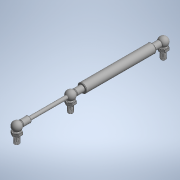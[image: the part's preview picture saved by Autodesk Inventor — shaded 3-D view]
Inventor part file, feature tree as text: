
AUTODESK INVENTOR PART (.ipt)
format: ipt  version: 2020 (Build 240168000, 168)  size: 1,038,848 bytes
history: native  units: mm (DEFAULTED — no unit token found)
features: boolean_combine x4, other x2, fillet x1
ambient origin geometry x8: Origin, YZ Plane, XZ Plane, XY Plane, X Axis, Y Axis, Z Axis, Center Point
bodies: Solid1 (feature_tree), Solid2 (feature_tree), Solid3 (feature_tree), Solid4 (feature_tree), Solid5 (feature_tree), Solid6 (feature_tree), Solid7 (feature_tree)
feature tree (7):
  other  "Cut-Revolve1"
  boolean_combine  "Combine1"
  boolean_combine  "Combine2"
  fillet  "Fillet1"  [1 undecoded]
  other  "LPattern1[1]"
  boolean_combine  "Combine7"
  boolean_combine  "Combine8"
note: 1 required parameter value undecoded (feature->parameter linkage not recoverable at this tier; creation-order binding heuristic only, values carry confidence <= 0.55)
